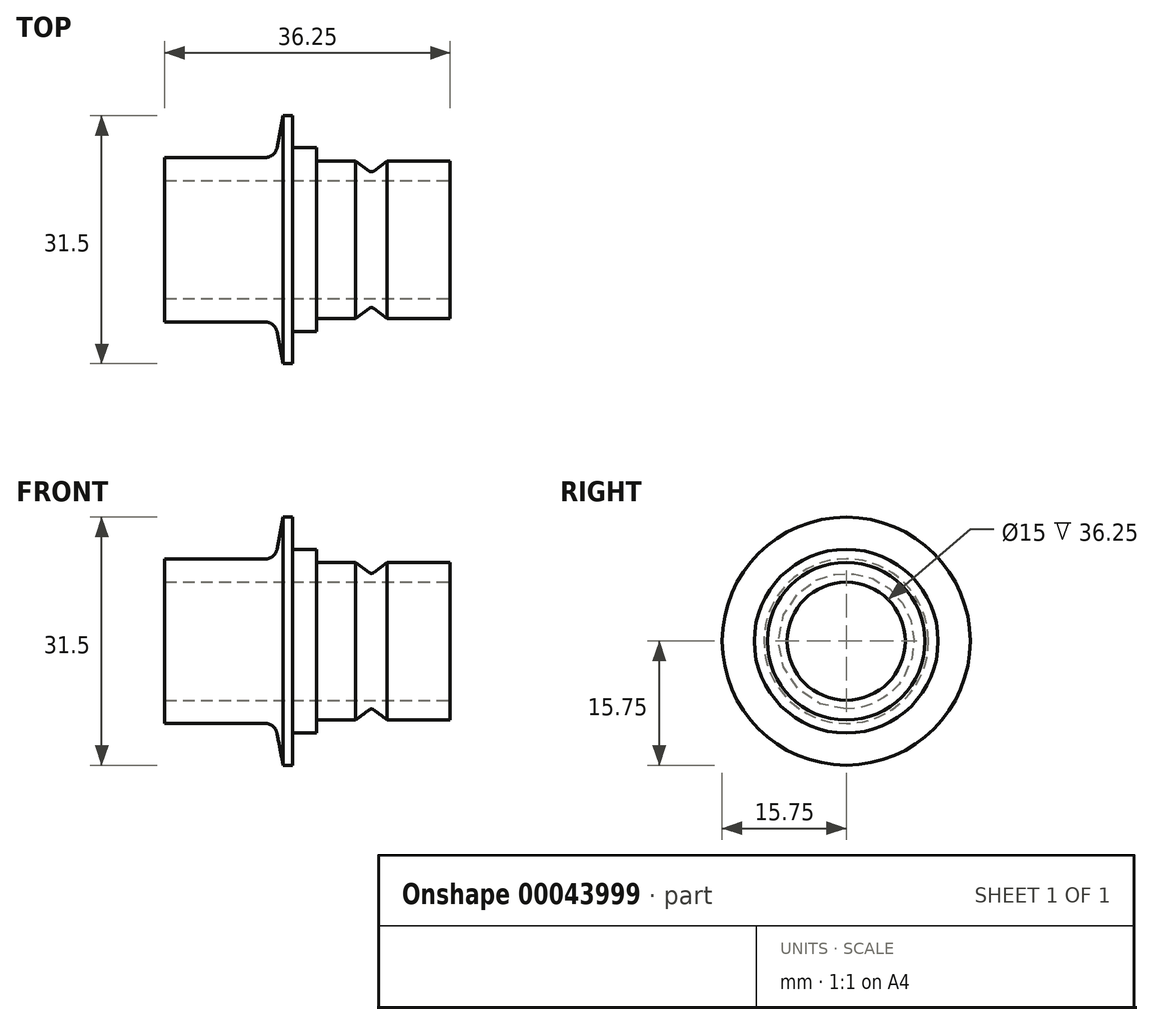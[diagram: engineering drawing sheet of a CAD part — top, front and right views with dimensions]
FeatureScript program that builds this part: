
annotation { "Feature Type Name" : "Feature", "Feature Type Description" : "" }
export const myFeature = defineFeature(function(context is Context, id is Id, definition is map)
    precondition{}
    {
        {
            var Q0;
            Q0=qCreatedBy(makeId("Front.planeOp"),FACE);
            var sketch = newSketch(context, id + "F0", { "sketchPlane" : qUnion([Q0])});
            skLineSegment(sketch, "E0", {"start": v(0, 0) * mm, "end": v(-22, 0) * mm});
            skLineSegment(sketch, "E1", {"start": v(0, 7.5) * mm, "end": v(-36.25, 7.5) * mm});
            skLineSegment(sketch, "E2", {"start": v(0, 7.5) * mm, "end": v(0, 10) * mm});
            skLineSegment(sketch, "E3", {"start": v(0, 10) * mm, "end": v(-8, 10) * mm});
            skLineSegment(sketch, "E4", {"start": v(-20, 11.93) * mm, "end": v(-20, 15.75) * mm});
            skLineSegment(sketch, "E5", {"start": v(-20, 15.75) * mm, "end": v(-21.2, 15.75) * mm});
            skLineSegment(sketch, "E6", {"start": v(-23.48, 10.45) * mm, "end": v(-36.25, 10.45) * mm});
            skLineSegment(sketch, "E7", {"start": v(-36.25, 10.45) * mm, "end": v(-36.25, 7.5) * mm});
            skLineSegment(sketch, "E8", {"start": v(-21.2, 15.75) * mm, "end": v(-22.01, 11.66) * mm});
            skLineSegment(sketch, "E9.bottom", {"start": v(-19.75, 11.68) * mm, "end": v(-17, 11.68) * mm});
            skLineSegment(sketch, "E9.right", {"start": v(-17, 11.68) * mm, "end": v(-17, 10.25) * mm});
            skLineSegment(sketch, "E10", {"start": v(-8, 10) * mm, "end": v(-9.7, 8.73) * mm});
            skLineSegment(sketch, "E11", {"start": v(-10.3, 8.73) * mm, "end": v(-12, 10) * mm});
            skLineSegment(sketch, "E12.trimOffspring", {"start": v(-12, 10) * mm, "end": v(-16.75, 10) * mm});
            skPoint(sketch, "E13.visualSharp", {"position": v(-10, 8.5) * mm});
            skArc(sketch, "E13.filletArc", {"start": v(-10.3, 8.73) * mm, "mid": v(-10, 8.62) * mm, "end": v(-9.7, 8.72) * mm});
            skPoint(sketch, "E14.visualSharp", {"position": v(-22.25, 10.45) * mm});
            skArc(sketch, "E14.filletArc", {"start": v(-23.48, 10.45) * mm, "mid": v(-22.53, 10.8) * mm, "end": v(-22.01, 11.66) * mm});
            skPoint(sketch, "E15.visualSharp", {"position": v(-20, 11.68) * mm});
            skArc(sketch, "E15.filletArc", {"start": v(-20, 11.93) * mm, "mid": v(-19.93, 11.75) * mm, "end": v(-19.75, 11.68) * mm});
            skPoint(sketch, "E16.visualSharp", {"position": v(-17, 10) * mm});
            skArc(sketch, "E16.filletArc", {"start": v(-17, 10.25) * mm, "mid": v(-16.93, 10.07) * mm, "end": v(-16.75, 10) * mm});
            skSolve(sketch);
        }
        {
            var Q0;
            Q0=makeQuery(id+"F0.imprint","IMPRINT",FACE,{"disambiguationData":[TD([[makeQuery(id+"F0.imprint","IMPRINT",EDGE,{"derivedFrom":sQuery(id+"F0.wireOp",EDGE,"E1")}),-1.0]])]});
            var Q1;
            Q1=sQuery(id+"F0.wireOp",EDGE,"E0");
            revolve(context, id + "F1", {"entities" : qUnion([Q0]), "axis" : qUnion([Q1]), "revolveType" : RevolveType.FULL});
        }
    });
